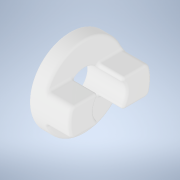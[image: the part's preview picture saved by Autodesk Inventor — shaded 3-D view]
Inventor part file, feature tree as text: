
AUTODESK INVENTOR PART (.ipt)
format: ipt  version: 2020 (Build 240168000, 168)  size: 308,224 bytes
history: native  units: mm
features: fillet x5, sketch x2, extrude x2, hole x1
ambient origin geometry x8: Origin, YZ Plane, XZ Plane, XY Plane, X Axis, Y Axis, Z Axis, Center Point
bodies: Solid1 (feature_tree)
feature tree (10):
  sketch  "Sketch1"  dims[d0=8.0mm d1=2.75mm]
  extrude  "Extrusion1"  Depth=2.75mm
  extrude  "Extrusion2"  Depth=2.5mm TaperAngle=0.0deg
  hole  "Hole1"  [1 undecoded]
  fillet  "Fillet1"  Radius=0.5mm
  fillet  "Fillet2"  Radius=0.25mm
  fillet  "Fillet3"  Radius=0.25mm
  fillet  "Fillet4"  Radius=0.125mm
  fillet  "Fillet5"  [1 undecoded]
  sketch  "Sketch2"  dims[d2=1.5mm d3=0.0mm d4=2.5mm d5=0.0mm d6=3.2mm d7=6.0mm d8=4.0mm d9=2.0mm d10=90.0deg d11=8.0mm d12=20.594885mm d13=0.25mm d14=0.5mm d15=0.25mm d16=0.25mm d17=0.125mm]
note: 2 required parameter values undecoded (feature->parameter linkage not recoverable at this tier; creation-order binding heuristic only, values carry confidence <= 0.55)
